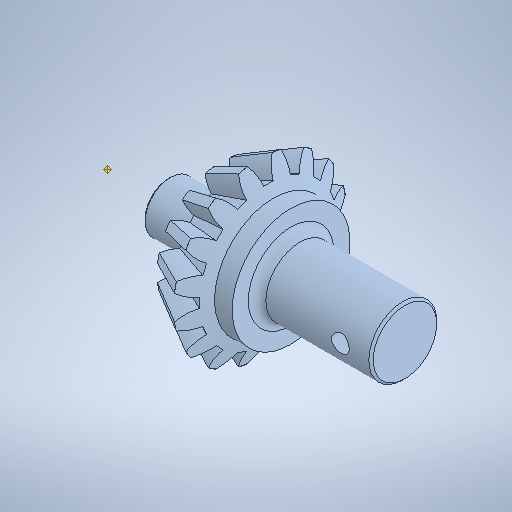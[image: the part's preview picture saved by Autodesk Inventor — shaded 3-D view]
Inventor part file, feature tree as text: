
AUTODESK INVENTOR PART (.ipt)
format: ipt  version: 2025.1 (Build 291241000, 241)  size: 514,560 bytes
history: native  units: in
note: dims shown in document units (in); Inventor stores cm internally (conversion verified against a paired STEP export)
features: plane x6, sketch x6, extrude x3, revolve x2, pattern_circular x1, chamfer x1, fillet x1
ambient origin geometry x8: Origin, YZ Plane, XZ Plane, XY Plane, X Axis, Y Axis, Z Axis, Center Point
bodies: Solid1 (feature_tree)
feature tree (20):
  revolve  "Revolution1"  [1 undecoded]
  plane  "Work Plane2"
  plane  "Work Plane5"
  extrude  "Extrusion6"  Depth=0.0787in
  pattern_circular  "Circular Pattern2"  Count=4  [1 undecoded]
  plane  "Work Plane7"
  plane  "Work Plane6"
  sketch  "Sketch11"  dims[d5=0.3937in d9=1.5748in]
  revolve  "Revolution3"  [1 undecoded]
  extrude  "Extrusion8"  Depth=0.0787in
  chamfer  "Chamfer3"  Distance=1.4961in
  fillet  "Congé5"  Radius=0.3543in
  extrude  "Extrusion15"  Depth=0.0787in
  sketch  "Sketch1"  dims[d0=3.1496in d1=0.1825in]
  plane  "Work Plane1"
  plane  "Work Plane4"
  sketch  "Sketch8"  dims[d2=0.0787in d3=0.0945in]
  sketch  "Sketch12"  dims[d10=90.0deg d11=0.162in d12=1.5748in]
  sketch  "Sketch13"  dims[d43=0.7043in d47=1.4085in d48=1.4961in d49=0.3543in d50=-0.4359in d51=1.5748in d53=0.0787in d54=0.0691in d56=0.4724in d57=-0.0197in d58=6.2992in d59=360.0deg d63=0.1297in d82=0.0875in d83=-0.0875in d84=1.4086in d89=1.0236in d90=0.315in d91=0.1181in d92=90.0deg d93=0.4567in d94=0.4724in d95=0.0in d96=0.3051in d105=0.0197in d106=0.0787in d107=45.0deg d130=0.1575in d131=0.5292in d146=0.0787in d147=0.2756in d148=0.1575in d149=0.0in d150=0.0in]
  sketch  "Esquisse23"
note: 3 required parameter values undecoded (feature->parameter linkage not recoverable at this tier; creation-order binding heuristic only, values carry confidence <= 0.55)